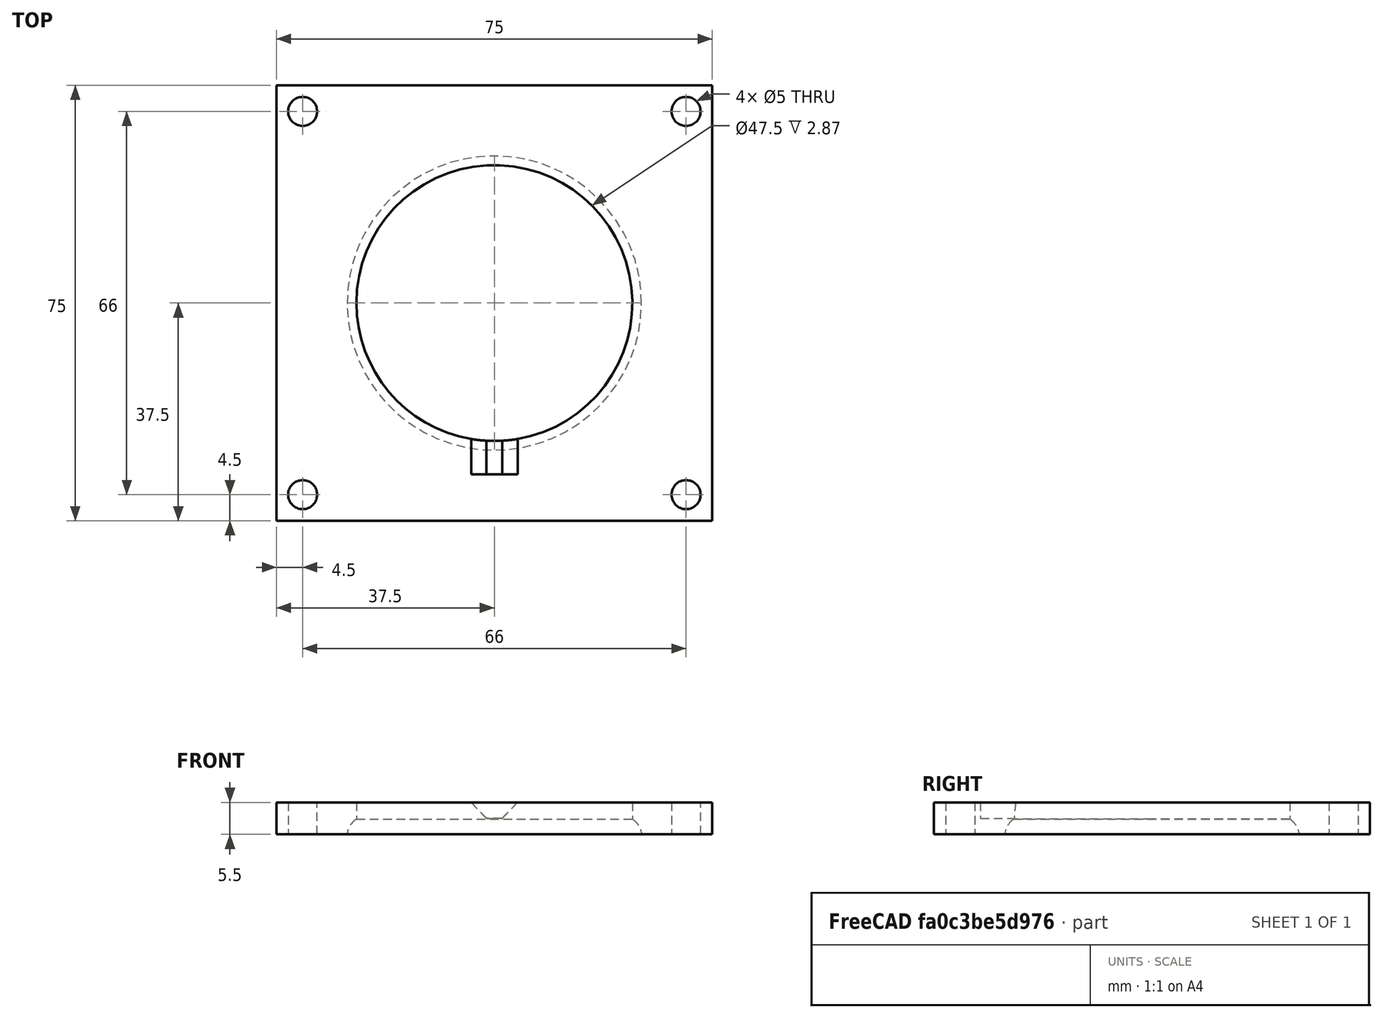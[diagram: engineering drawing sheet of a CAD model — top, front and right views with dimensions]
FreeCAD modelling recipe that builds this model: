
FCSTD DOCUMENT  (FreeCAD 0.18R16110 (Git))
Label: hubbase
License: All rights reserved
LicenseURL: http://en.wikipedia.org/wiki/All_rights_reserved
objects: Sketcher::SketchObject×3, Mesh::Feature×3, Part::Extrusion×2, Part::Cut×2, Part::Revolution×1
note: 8 computed .brp shape members not serialized (recipe doc carries the construction recipe); baked Part::Feature solids carry a one-line shape summary decoded from their .brp

FEATURE [Sketcher::SketchObject] Sketch
  Placement = pos=(0,0,-12.5) rot=(0,0,1;0rad)
  sketch-geometry (10):
    g0: LineSegment StartX=-37.5 StartY=37.5 StartZ=0 EndX=37.5 EndY=37.5 EndZ=0
    g1: LineSegment StartX=37.5 StartY=37.5 StartZ=0 EndX=37.5 EndY=-37.5 EndZ=0
    g2: LineSegment StartX=37.5 StartY=-37.5 StartZ=0 EndX=-37.5 EndY=-37.5 EndZ=0
    g3: LineSegment StartX=-37.5 StartY=-37.5 StartZ=0 EndX=-37.5 EndY=37.5 EndZ=0
    g4: Circle CenterX=-33 CenterY=33 CenterZ=0 NormalX=0 NormalY=0 NormalZ=1 AngleXU=0 Radius=2.5
    g5: Circle CenterX=33 CenterY=33 CenterZ=0 NormalX=0 NormalY=0 NormalZ=1 AngleXU=0 Radius=2.5
    g6: Circle CenterX=-33 CenterY=-33 CenterZ=0 NormalX=0 NormalY=0 NormalZ=1 AngleXU=0 Radius=2.5
    g7: Circle CenterX=33 CenterY=-33 CenterZ=0 NormalX=0 NormalY=0 NormalZ=1 AngleXU=0 Radius=2.5
    g8: LineSegment [constr] StartX=33 StartY=37.5 StartZ=0 EndX=33 EndY=35.5 EndZ=0
    g9: LineSegment [constr] StartX=35.5 StartY=33 StartZ=0 EndX=37.5 EndY=33 EndZ=0
  constraints (27):
    c: Coincident(g0,g1)
    c: Coincident(g1,g2)
    c: Coincident(g2,g3)
    c: Coincident(g3,g0)
    c: Horizontal(g2)
    c: Vertical(g1)
    c: Symmetric(g0,g0,g-2)
    c: Symmetric(g0,g2,g-1)
    c: Distance(g0) = 75
    c: Distance(g3) = 75
    c: Symmetric(g4,g5,g-2)
    c: Symmetric(g6,g4,g-1)
    c: Symmetric(g7,g6,g-2)
    c: Radius(g5) = 2.5
    c: Radius(g4) = 2.5
    c: Radius(g6) = 2.5
    c: Radius(g7) = 2.5
    c: PointOnObject(g8,g0)
    c: PointOnObject(g8,g5)
    c: Vertical(g8)
    c: Distance(g8) = 2
    c: PointOnObject(g9,g5)
    c: PointOnObject(g9,g1)
    c: Horizontal(g9)
    c: Distance(g9) = 2
    c: Perpendicular(g5,g9)
    c: Perpendicular(g5,g8)
FEATURE [Part::Extrusion] Extrude
  Base = -> Sketch
  Dir = (0,0,1)
  DirMode = 2
  FaceMakerClass = Part::FaceMakerBullseye
  LengthFwd = 5.5
  LengthRev = 0
  Solid = true
  Symmetric = false
FEATURE [Sketcher::SketchObject] Sketch001
  MapMode = 3
  Placement = pos=(0,0,-12.5) rot=(1,0,0;1.5708rad)
  Support = -> [Sketch]
  sketch-geometry (5):
    g0: LineSegment StartX=0 StartY=5.5 StartZ=0 EndX=-23.75 EndY=5.5 EndZ=0
    g1: LineSegment StartX=-23.75 StartY=5.5 StartZ=0 EndX=-23.75 EndY=2.63 EndZ=0
    g2: LineSegment StartX=-25.3277 StartY=1e-16 StartZ=0 EndX=0 EndY=0 EndZ=0
    g3: LineSegment StartX=0 StartY=0 StartZ=0 EndX=0 EndY=5.5 EndZ=0
    g4: ArcOfCircle CenterX=-21.8409 CenterY=-0.303506 CenterZ=0 NormalX=0 NormalY=0 NormalZ=1 AngleXU=0 Radius=3.5 StartAngle=2.14772 EndAngle=3.05477
  constraints (15):
    c: PointOnObject(g0,g-2)
    c: Horizontal(g0)
    c: Coincident(g0,g1)
    c: Vertical(g1)
    c: PointOnObject(g2,g-1)
    c: Coincident(g2,g-1)
    c: Coincident(g2,g3)
    c: Coincident(g3,g0)
    c: DistanceY(g3,g3) = 5.5
    c: DistanceX(g0,g0) = 23.75
    c: DistanceY(g1,g1) = 2.87
    c: Coincident(g4,g1)
    c: Coincident(g4,g2)
    c: Radius(g4) = 3.5
    c: Angle(g4) = 0.907048
FEATURE [Part::Revolution] Revolve
  Angle = 360
  Axis = (0,0,1)
  Base = (0,0,0)
  FaceMakerClass = Part::FaceMakerBullseye
  Solid = true
  Source = -> Sketch001
  Symmetric = false
FEATURE [Part::Cut] Cut
  Base = -> Extrude
  Tool = -> Revolve
FEATURE [Sketcher::SketchObject] Sketch002
  MapMode = 5
  Placement = pos=(0,-37.5,0) rot=(1,0,0;1.5708rad)
  Support = -> [Cut]
  sketch-geometry (5):
    g0: LineSegment StartX=-4 StartY=-10 StartZ=0 EndX=4 EndY=-10 EndZ=0
    g1: LineSegment StartX=4 StartY=-10 StartZ=0 EndX=1.34436 EndY=-7.25 EndZ=0
    g2: LineSegment StartX=1.34436 StartY=-7.25 StartZ=0 EndX=-1.34436 EndY=-7.25 EndZ=0
    g3: LineSegment StartX=-1.34436 StartY=-7.25 StartZ=0 EndX=-4 EndY=-10 EndZ=0
    g4: LineSegment [constr] StartX=1.34436 StartY=-7.25 StartZ=0 EndX=1.34436 EndY=-10 EndZ=0
  constraints (14):
    c: Coincident(g0,g1)
    c: Coincident(g1,g2)
    c: Horizontal(g2)
    c: Coincident(g2,g3)
    c: Coincident(g3,g0)
    c: Angle(g0,g3) = 0.802851
    c: Angle(g1,g0) = 0.802851
    c: Symmetric(g0,g0,g-2)
    c: DistanceX(g0,g0) = 8
    c: Coincident(g4,g1)
    c: PointOnObject(g4,g0)
    c: Vertical(g4)
    c: DistanceY(g4,g4) = 2.75
    c: DistanceY(g0) = -10
FEATURE [Part::Extrusion] Extrude002
  Base = -> Sketch002
  Dir = (0,-1,2e-16)
  DirMode = 2
  FaceMakerClass = Part::FaceMakerBullseye
  LengthFwd = 8
  LengthRev = 0
  Placement = pos=(0,8,-17) rot=(0,1,0;3.14159rad)
  Reversed = true
  Solid = true
  Symmetric = false
FEATURE [Mesh::Feature] square2_4  label="square2.4"
  Placement = pos=(0.35,39.8,-14) rot=(1,0,0;1.5708rad)
FEATURE [Mesh::Feature] handlecurve
  Placement = pos=(1.9,31,-13) rot=(0.57735,0.57735,-0.57735;4.18879rad)
FEATURE [Mesh::Feature] square2_4001  label="square2.005"
  Placement = pos=(0.35,42,-14) rot=(1,0,0;1.5708rad)
FEATURE [Part::Cut] Cut001
  Base = -> Cut
  Tool = -> Extrude002
